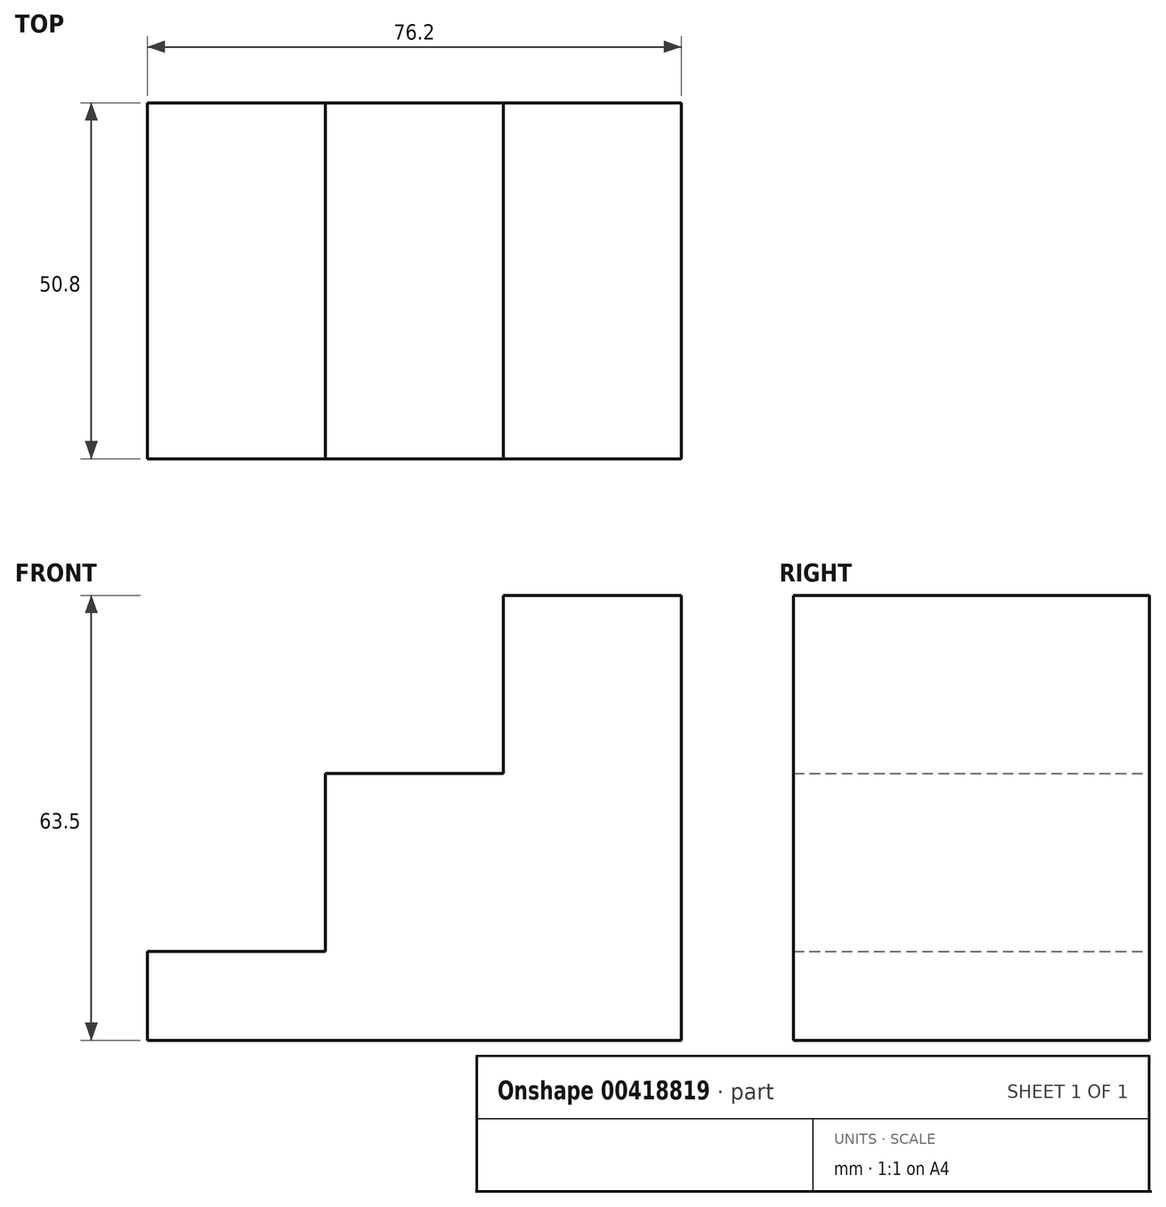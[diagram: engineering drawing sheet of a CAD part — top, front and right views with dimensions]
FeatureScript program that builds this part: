
annotation { "Feature Type Name" : "Feature", "Feature Type Description" : "" }
export const myFeature = defineFeature(function(context is Context, id is Id, definition is map)
    precondition{}
    {
        {
            var Q0;
            Q0=qCreatedBy(makeId("Front.planeOp"),FACE);
            var sketch = newSketch(context, id + "F0", { "sketchPlane" : qUnion([Q0])});
            skLineSegment(sketch, "E0", {"start": v(0, 0) * mm, "end": v(-76.2, 0) * mm});
            skLineSegment(sketch, "E1", {"start": v(-76.2, 0) * mm, "end": v(-76.2, 12.7) * mm});
            skLineSegment(sketch, "E2", {"start": v(-76.2, 12.7) * mm, "end": v(-50.8, 12.7) * mm});
            skLineSegment(sketch, "E3", {"start": v(-50.8, 12.7) * mm, "end": v(-50.8, 38.1) * mm});
            skLineSegment(sketch, "E4", {"start": v(-50.8, 38.1) * mm, "end": v(-25.4, 38.1) * mm});
            skLineSegment(sketch, "E5", {"start": v(-25.4, 38.1) * mm, "end": v(-25.4, 63.5) * mm});
            skLineSegment(sketch, "E6", {"start": v(-25.4, 63.5) * mm, "end": v(0, 63.5) * mm});
            skLineSegment(sketch, "E7", {"start": v(0, 63.5) * mm, "end": v(0, 0) * mm});
            skSolve(sketch);
        }
        {
            var Q0;
            Q0=makeQuery(id+"F0.imprint","IMPRINT",FACE,{"disambiguationData":[TD([[makeQuery(id+"F0.imprint","IMPRINT",EDGE,{"derivedFrom":sQuery(id+"F0.wireOp",EDGE,"E0")}),-1.0]])]});
            extrude(context, id + "F1", {"entities" : qUnion([Q0]), "depth" : 50.8 * mm});
        }
    });
